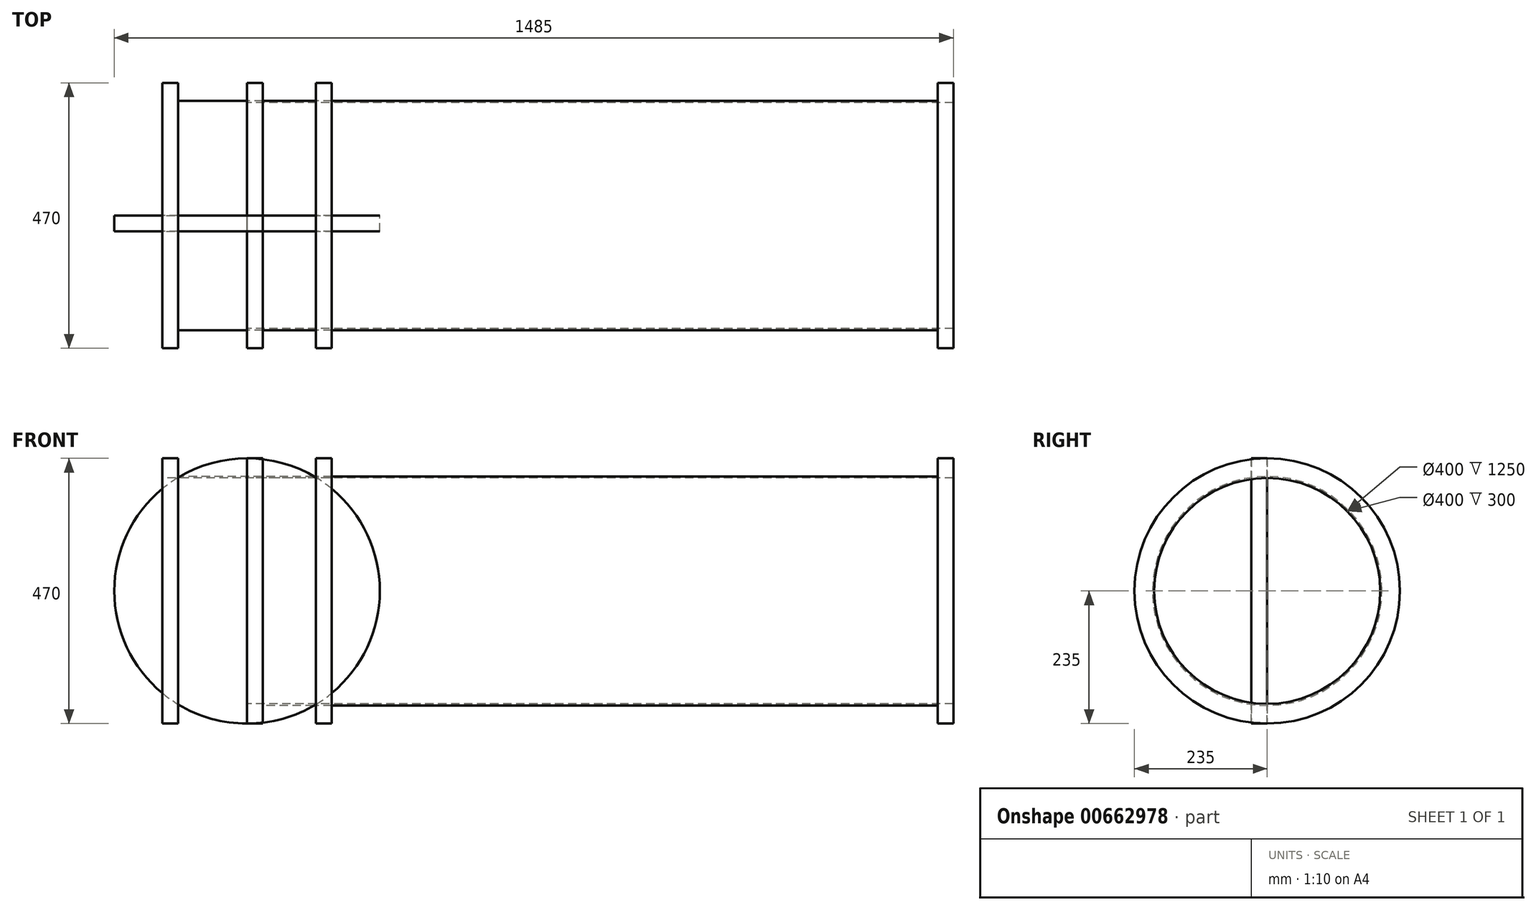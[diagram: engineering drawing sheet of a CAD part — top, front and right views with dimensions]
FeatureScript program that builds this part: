
annotation { "Feature Type Name" : "Feature", "Feature Type Description" : "" }
export const myFeature = defineFeature(function(context is Context, id is Id, definition is map)
    precondition{}
    {
        {
            var Q0;
            Q0=qCreatedBy(makeId("Front.planeOp"),FACE);
            var sketch = newSketch(context, id + "F0", { "sketchPlane" : qUnion([Q0])});
            skLineSegment(sketch, "E0", {"start": v(0, 200) * mm, "end": v(1250, 200) * mm});
            skLineSegment(sketch, "E1", {"start": v(1250, 200) * mm, "end": v(1250, 235) * mm});
            skLineSegment(sketch, "E2", {"start": v(1250, 235) * mm, "end": v(1222, 235) * mm});
            skLineSegment(sketch, "E3", {"start": v(1222, 235) * mm, "end": v(1222, 203) * mm});
            skLineSegment(sketch, "E4", {"start": v(1222, 203) * mm, "end": v(28, 203) * mm});
            skLineSegment(sketch, "E5", {"start": v(28, 203) * mm, "end": v(28, 235) * mm});
            skLineSegment(sketch, "E6", {"start": v(28, 235) * mm, "end": v(0, 235) * mm});
            skLineSegment(sketch, "E7", {"start": v(0, 235) * mm, "end": v(0, 200) * mm});
            skSolve(sketch);
        }
        {
            var Q0;
            Q0=qCreatedBy(makeId("Front.planeOp"),FACE);
            var sketch = newSketch(context, id + "F1", { "sketchPlane" : qUnion([Q0])});
            skLineSegment(sketch, "E8", {"start": v(-72.7, 0) * mm, "end": v(0, 0) * mm, "construction": true});
            skSolve(sketch);
        }
        {
            var Q0;
            Q0=makeQuery(id+"F0.imprint","IMPRINT",FACE,{"disambiguationData":[TD([[makeQuery(id+"F0.imprint","IMPRINT",EDGE,{"derivedFrom":sQuery(id+"F0.wireOp",EDGE,"E0")}),1.0]])]});
            var Q1;
            Q1=sQuery(id+"F1.wireOp",EDGE,"E8");
            revolve(context, id + "F2", {"surfaceOperationType" : NewSurfaceOperationType.NEW, "entities" : qUnion([Q0]), "axis" : qUnion([Q1]), "revolveType" : RevolveType.FULL});
        }
        {
            var Q0;
            Q0=makeQuery(id+"F2.opRevolve","SWEPT_FACE",FACE,{"disambiguationData":[OSD([sQuery(id+"F0.wireOp",EDGE,"E7")])]});
            var sketch = newSketch(context, id + "F3", { "sketchPlane" : qUnion([Q0])});
            skCircle(sketch, "E9", {"center": v(0, 0) * mm, "radius": 218.95 * mm, "construction": true});
            skPoint(sketch, "E10", {"position": v(218.95, 0) * mm});
            skLineSegment(sketch, "E11", {"start": v(0, 0) * mm, "end": v(218.95, 0) * mm, "construction": true});
            skPoint(sketch, "E12.1.0", {"position": v(216.25, 34.25) * mm});
            skPoint(sketch, "E12.2.0", {"position": v(208.23, 67.66) * mm});
            skPoint(sketch, "E12.3.0", {"position": v(195.09, 99.4) * mm});
            skPoint(sketch, "E12.4.0", {"position": v(177.13, 128.7) * mm});
            skPoint(sketch, "E12.5.0", {"position": v(154.82, 154.82) * mm});
            skPoint(sketch, "E12.6.0", {"position": v(128.7, 177.13) * mm});
            skPoint(sketch, "E12.7.0", {"position": v(99.4, 195.09) * mm});
            skPoint(sketch, "E12.8.0", {"position": v(67.66, 208.23) * mm});
            skPoint(sketch, "E12.9.0", {"position": v(34.25, 216.25) * mm});
            skPoint(sketch, "E12.10.0", {"position": v(0, 218.95) * mm});
            skPoint(sketch, "E12.11.0", {"position": v(-34.25, 216.25) * mm});
            skPoint(sketch, "E12.12.0", {"position": v(-67.66, 208.23) * mm});
            skPoint(sketch, "E12.13.0", {"position": v(-99.4, 195.09) * mm});
            skPoint(sketch, "E12.14.0", {"position": v(-128.7, 177.13) * mm});
            skPoint(sketch, "E12.15.0", {"position": v(-154.82, 154.82) * mm});
            skPoint(sketch, "E12.16.0", {"position": v(-177.13, 128.7) * mm});
            skPoint(sketch, "E12.17.0", {"position": v(-195.09, 99.4) * mm});
            skPoint(sketch, "E12.18.0", {"position": v(-208.23, 67.66) * mm});
            skPoint(sketch, "E12.19.0", {"position": v(-216.25, 34.25) * mm});
            skPoint(sketch, "E12.20.0", {"position": v(-218.95, 0) * mm});
            skPoint(sketch, "E12.21.0", {"position": v(-216.25, -34.25) * mm});
            skPoint(sketch, "E12.22.0", {"position": v(-208.23, -67.66) * mm});
            skPoint(sketch, "E12.23.0", {"position": v(-195.09, -99.4) * mm});
            skPoint(sketch, "E12.24.0", {"position": v(-177.13, -128.7) * mm});
            skPoint(sketch, "E12.25.0", {"position": v(-154.82, -154.82) * mm});
            skPoint(sketch, "E12.26.0", {"position": v(-128.7, -177.13) * mm});
            skPoint(sketch, "E12.27.0", {"position": v(-99.4, -195.09) * mm});
            skPoint(sketch, "E12.28.0", {"position": v(-67.66, -208.23) * mm});
            skPoint(sketch, "E12.29.0", {"position": v(-34.25, -216.25) * mm});
            skPoint(sketch, "E12.30.0", {"position": v(0, -218.95) * mm});
            skPoint(sketch, "E12.31.0", {"position": v(34.25, -216.25) * mm});
            skPoint(sketch, "E12.32.0", {"position": v(67.66, -208.23) * mm});
            skPoint(sketch, "E12.33.0", {"position": v(99.4, -195.09) * mm});
            skPoint(sketch, "E12.34.0", {"position": v(128.7, -177.13) * mm});
            skPoint(sketch, "E12.35.0", {"position": v(154.82, -154.82) * mm});
            skPoint(sketch, "E12.36.0", {"position": v(177.13, -128.7) * mm});
            skPoint(sketch, "E12.37.0", {"position": v(195.09, -99.4) * mm});
            skPoint(sketch, "E12.38.0", {"position": v(208.23, -67.66) * mm});
            skPoint(sketch, "E12.39.0", {"position": v(216.25, -34.25) * mm});
            skSolve(sketch);
        }
        {
            var Q0;
            Q0=qCreatedBy(makeId("Front.planeOp"),FACE);
            var sketch = newSketch(context, id + "F4", { "sketchPlane" : qUnion([Q0])});
            skLineSegment(sketch, "E13", {"start": v(-150, 200) * mm, "end": v(150, 200) * mm});
            skLineSegment(sketch, "E14", {"start": v(150, 200) * mm, "end": v(150, 235) * mm});
            skLineSegment(sketch, "E15", {"start": v(150, 235) * mm, "end": v(122, 235) * mm});
            skLineSegment(sketch, "E16", {"start": v(122, 235) * mm, "end": v(122, 203) * mm});
            skLineSegment(sketch, "E17", {"start": v(122, 203) * mm, "end": v(-122, 203) * mm});
            skLineSegment(sketch, "E18", {"start": v(-122, 203) * mm, "end": v(-122, 235) * mm});
            skLineSegment(sketch, "E19", {"start": v(-122, 235) * mm, "end": v(-150, 235) * mm});
            skLineSegment(sketch, "E20", {"start": v(-150, 235) * mm, "end": v(-150, 200) * mm});
            skSolve(sketch);
        }
        {
            var Q0;
            Q0=makeQuery(id+"F4.imprint","IMPRINT",FACE,{"disambiguationData":[TD([[makeQuery(id+"F4.imprint","IMPRINT",EDGE,{"derivedFrom":sQuery(id+"F4.wireOp",EDGE,"E13")}),1.0]])]});
            var Q1;
            Q1=sQuery(id+"F1.wireOp",EDGE,"E8");
            revolve(context, id + "F5", {"surfaceOperationType" : NewSurfaceOperationType.NEW, "entities" : qUnion([Q0]), "axis" : qUnion([Q1]), "revolveType" : RevolveType.FULL});
        }
        {
            var Q0;
            Q0=qCreatedBy(makeId("Front.planeOp"),FACE);
            var sketch = newSketch(context, id + "F6", { "sketchPlane" : qUnion([Q0])});
            skCircle(sketch, "E21", {"center": v(0, 0) * mm, "radius": 235 * mm});
            skSolve(sketch);
        }
        {
            var Q0;
            Q0=makeQuery(id+"F6.imprint","IMPRINT",FACE,{"disambiguationData":[TD([[makeQuery(id+"F6.imprint","IMPRINT",EDGE,{"derivedFrom":sQuery(id+"F6.wireOp",EDGE,"E21")}),1.0]])]});
            extrude(context, id + "F7", {"entities" : qUnion([Q0]), "depth" : 28 * mm, "offsetDistance" : 25 * mm});
        }
    });
